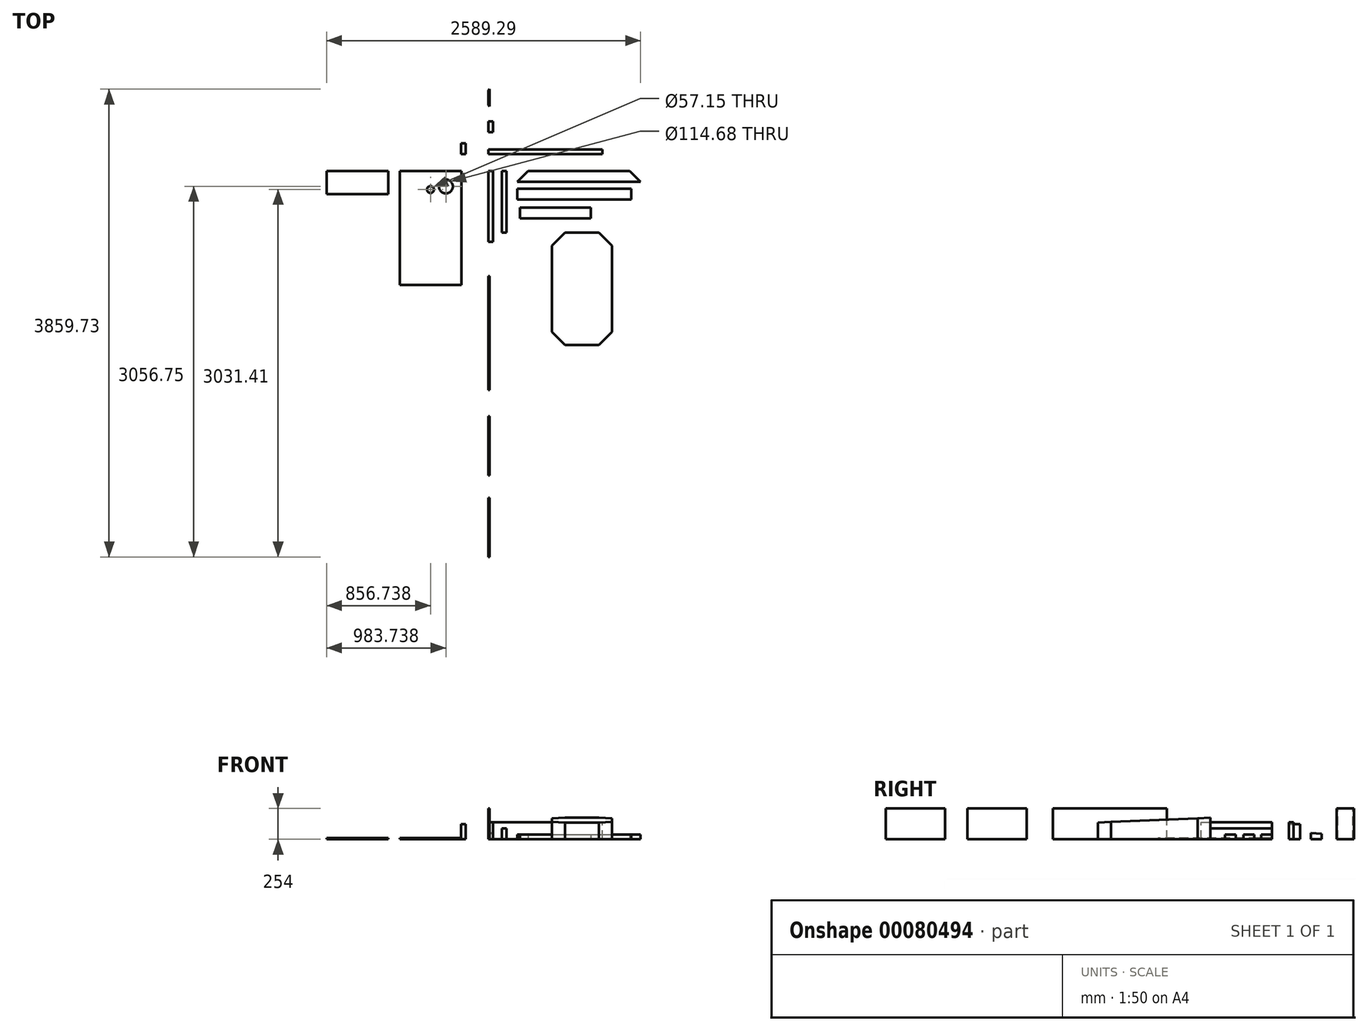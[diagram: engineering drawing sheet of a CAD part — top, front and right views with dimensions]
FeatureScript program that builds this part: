
annotation { "Feature Type Name" : "Feature", "Feature Type Description" : "" }
export const myFeature = defineFeature(function(context is Context, id is Id, definition is map)
    precondition{}
    {
        {
            var Q0;
            Q0=qCreatedBy(makeId("Front.planeOp"),FACE);
            var sketch = newSketch(context, id + "F0", { "sketchPlane" : qUnion([Q0])});
            skLineSegment(sketch, "E0.bottom", {"start": v(0, 0) * mm, "end": v(38.1, 0) * mm});
            skLineSegment(sketch, "E0.top", {"start": v(0, 139.7) * mm, "end": v(38.1, 139.7) * mm});
            skLineSegment(sketch, "E0.left", {"start": v(0, 0) * mm, "end": v(0, 139.7) * mm});
            skLineSegment(sketch, "E0.right", {"start": v(38.1, 0) * mm, "end": v(38.1, 139.7) * mm});
            skSolve(sketch);
        }
        {
            var Q0;
            Q0=makeQuery(id+"F0.imprint","IMPRINT",FACE,{"disambiguationData":[TD([[makeQuery(id+"F0.imprint","IMPRINT",EDGE,{"derivedFrom":sQuery(id+"F0.wireOp",EDGE,"E0.bottom")}),1.0]])]});
            extrude(context, id + "F1", {"entities" : qUnion([Q0]), "depth" : 584.2 * mm});
        }
        {
            var Q0;
            Q0=qCreatedBy(makeId("Right.planeOp"),FACE);
            var sketch = newSketch(context, id + "F2", { "sketchPlane" : qUnion([Q0])});
            skLineSegment(sketch, "E1.bottom", {"start": v(138.59, 0) * mm, "end": v(176.69, 0) * mm});
            skLineSegment(sketch, "E1.top", {"start": v(138.59, 139.7) * mm, "end": v(176.69, 139.7) * mm});
            skLineSegment(sketch, "E1.left", {"start": v(138.59, 0) * mm, "end": v(138.59, 139.7) * mm});
            skLineSegment(sketch, "E1.right", {"start": v(176.69, 0) * mm, "end": v(176.69, 139.7) * mm});
            skSolve(sketch);
        }
        {
            var Q0;
            Q0=makeQuery(id+"F2.imprint","IMPRINT",FACE,{"disambiguationData":[TD([[makeQuery(id+"F2.imprint","IMPRINT",EDGE,{"derivedFrom":sQuery(id+"F2.wireOp",EDGE,"E1.bottom")}),1.0]])]});
            extrude(context, id + "F3", {"entities" : qUnion([Q0]), "depth" : 939.8 * mm});
        }
        {
            var Q0;
            Q0=qCreatedBy(makeId("Front.planeOp"),FACE);
            var sketch = newSketch(context, id + "F4", { "sketchPlane" : qUnion([Q0])});
            skLineSegment(sketch, "E2.bottom", {"start": v(110.06, 0) * mm, "end": v(148.16, 0) * mm});
            skLineSegment(sketch, "E2.top", {"start": v(110.06, 88.9) * mm, "end": v(148.16, 88.9) * mm});
            skLineSegment(sketch, "E2.left", {"start": v(110.06, 0) * mm, "end": v(110.06, 88.9) * mm});
            skLineSegment(sketch, "E2.right", {"start": v(148.16, 0) * mm, "end": v(148.16, 88.9) * mm});
            skSolve(sketch);
        }
        {
            var Q0;
            Q0=makeQuery(id+"F4.imprint","IMPRINT",FACE,{"disambiguationData":[TD([[makeQuery(id+"F4.imprint","IMPRINT",EDGE,{"derivedFrom":sQuery(id+"F4.wireOp",EDGE,"E2.bottom")}),1.0]])]});
            extrude(context, id + "F5", {"entities" : qUnion([Q0]), "depth" : 508 * mm});
        }
        {
            var Q0;
            Q0=qCreatedBy(makeId("Top.planeOp"),FACE);
            var sketch = newSketch(context, id + "F6", { "sketchPlane" : qUnion([Q0])});
            skLineSegment(sketch, "E3.bottom", {"start": v(-224.08, 0) * mm, "end": v(-732.08, 0) * mm});
            skLineSegment(sketch, "E3.top", {"start": v(-224.08, -939.8) * mm, "end": v(-732.08, -939.8) * mm});
            skLineSegment(sketch, "E3.left", {"start": v(-224.08, 0) * mm, "end": v(-224.08, -939.8) * mm});
            skLineSegment(sketch, "E3.right", {"start": v(-732.08, 0) * mm, "end": v(-732.08, -939.8) * mm});
            skSolve(sketch);
        }
        {
            var Q0;
            Q0=makeQuery(id+"F6.imprint","IMPRINT",FACE,{"disambiguationData":[TD([[makeQuery(id+"F6.imprint","IMPRINT",EDGE,{"derivedFrom":sQuery(id+"F6.wireOp",EDGE,"E3.bottom")}),1.0]])]});
            extrude(context, id + "F7", {"entities" : qUnion([Q0]), "depth" : 9.52 * mm});
        }
        {
            var Q0;
            Q0=qCreatedBy(makeId("Top.planeOp"),FACE);
            var sketch = newSketch(context, id + "F8", { "sketchPlane" : qUnion([Q0])});
            skLineSegment(sketch, "E4.bottom", {"start": v(-826.82, 0) * mm, "end": v(-1334.82, 0) * mm});
            skLineSegment(sketch, "E4.top", {"start": v(-826.82, -190.5) * mm, "end": v(-1334.82, -190.5) * mm});
            skLineSegment(sketch, "E4.left", {"start": v(-826.82, 0) * mm, "end": v(-826.82, -190.5) * mm});
            skLineSegment(sketch, "E4.right", {"start": v(-1334.82, 0) * mm, "end": v(-1334.82, -190.5) * mm});
            skSolve(sketch);
        }
        {
            var Q0;
            Q0=makeQuery(id+"F8.imprint","IMPRINT",FACE,{"disambiguationData":[TD([[makeQuery(id+"F8.imprint","IMPRINT",EDGE,{"derivedFrom":sQuery(id+"F8.wireOp",EDGE,"E4.bottom")}),1.0]])]});
            extrude(context, id + "F9", {"entities" : qUnion([Q0]), "depth" : 9.52 * mm});
        }
        {
            var Q0;
            Q0=qCreatedBy(makeId("Right.planeOp"),FACE);
            var sketch = newSketch(context, id + "F10", { "sketchPlane" : qUnion([Q0])});
            skLineSegment(sketch, "E5", {"start": v(-866.98, 0) * mm, "end": v(-866.98, 254) * mm});
            skLineSegment(sketch, "E6", {"start": v(-866.98, 254) * mm, "end": v(-1806.78, 254) * mm});
            skLineSegment(sketch, "E7", {"start": v(-1806.78, 254) * mm, "end": v(-1806.78, 0) * mm});
            skLineSegment(sketch, "E8", {"start": v(-1806.78, 0) * mm, "end": v(-1616.28, 0) * mm});
            skLineSegment(sketch, "E9", {"start": v(-1616.28, 0) * mm, "end": v(-1616.28, 0) * mm});
            skLineSegment(sketch, "E10", {"start": v(-1616.28, 0) * mm, "end": v(-866.98, 0) * mm});
            skSolve(sketch);
        }
        {
            var Q0;
            Q0=makeQuery(id+"F10.imprint","IMPRINT",FACE,{"disambiguationData":[TD([[makeQuery(id+"F10.imprint","IMPRINT",EDGE,{"derivedFrom":sQuery(id+"F10.wireOp",EDGE,"E5")}),1.0]])]});
            extrude(context, id + "F11", {"entities" : qUnion([Q0]), "depth" : 9.52 * mm});
        }
        {
            var Q0;
            Q0=qCreatedBy(makeId("Right.planeOp"),FACE);
            var sketch = newSketch(context, id + "F12", { "sketchPlane" : qUnion([Q0])});
            skLineSegment(sketch, "E11.bottom", {"start": v(-2022.5, 0) * mm, "end": v(-2511.45, 0) * mm});
            skLineSegment(sketch, "E11.top", {"start": v(-2022.5, 254) * mm, "end": v(-2511.45, 254) * mm});
            skLineSegment(sketch, "E11.left", {"start": v(-2022.5, 0) * mm, "end": v(-2022.5, 254) * mm});
            skLineSegment(sketch, "E11.right", {"start": v(-2511.45, 0) * mm, "end": v(-2511.45, 254) * mm});
            skSolve(sketch);
        }
        {
            var Q0;
            Q0=makeQuery(id+"F12.imprint","IMPRINT",FACE,{"disambiguationData":[TD([[makeQuery(id+"F12.imprint","IMPRINT",EDGE,{"derivedFrom":sQuery(id+"F12.wireOp",EDGE,"E11.bottom")}),-1.0]])]});
            extrude(context, id + "F13", {"entities" : qUnion([Q0]), "depth" : 9.52 * mm});
        }
        {
            var Q0;
            Q0=qCreatedBy(makeId("Right.planeOp"),FACE);
            var sketch = newSketch(context, id + "F14", { "sketchPlane" : qUnion([Q0])});
            skLineSegment(sketch, "E12.bottom", {"start": v(-2694.8, 0) * mm, "end": v(-3183.75, 0) * mm});
            skLineSegment(sketch, "E12.top", {"start": v(-2694.8, 254) * mm, "end": v(-3183.75, 254) * mm});
            skLineSegment(sketch, "E12.left", {"start": v(-2694.8, 0) * mm, "end": v(-2694.8, 254) * mm});
            skLineSegment(sketch, "E12.right", {"start": v(-3183.75, 0) * mm, "end": v(-3183.75, 254) * mm});
            skSolve(sketch);
        }
        {
            var Q0;
            Q0=makeQuery(id+"F14.imprint","IMPRINT",FACE,{"disambiguationData":[TD([[makeQuery(id+"F14.imprint","IMPRINT",EDGE,{"derivedFrom":sQuery(id+"F14.wireOp",EDGE,"E12.bottom")}),-1.0]])]});
            extrude(context, id + "F15", {"entities" : qUnion([Q0]), "depth" : 9.52 * mm});
        }
        {
            var Q0;
            Q0=qCreatedBy(makeId("Top.planeOp"),FACE);
            var sketch = newSketch(context, id + "F16", { "sketchPlane" : qUnion([Q0])});
            skLineSegment(sketch, "E13.bottom", {"start": v(327.37, 0) * mm, "end": v(1165.57, 0) * mm});
            skLineSegment(sketch, "E13.top", {"start": v(238.47, -88.9) * mm, "end": v(1254.47, -88.9) * mm});
            skLineSegment(sketch, "E14", {"start": v(238.47, -88.9) * mm, "end": v(327.37, 0) * mm});
            skLineSegment(sketch, "E15", {"start": v(1254.47, -88.9) * mm, "end": v(1165.57, 0) * mm});
            skSolve(sketch);
        }
        {
            var Q0;
            Q0=makeQuery(id+"F16.imprint","IMPRINT",FACE,{"disambiguationData":[TD([[makeQuery(id+"F16.imprint","IMPRINT",EDGE,{"derivedFrom":sQuery(id+"F16.wireOp",EDGE,"E13.bottom")}),-1.0]])]});
            extrude(context, id + "F17", {"entities" : qUnion([Q0]), "depth" : 38.1 * mm});
        }
        {
            var Q0;
            Q0=qCreatedBy(makeId("Top.planeOp"),FACE);
            var sketch = newSketch(context, id + "F18", { "sketchPlane" : qUnion([Q0])});
            skLineSegment(sketch, "E16.bottom", {"start": v(238.93, -146.3) * mm, "end": v(1178.73, -146.3) * mm});
            skLineSegment(sketch, "E16.top", {"start": v(238.93, -235.2) * mm, "end": v(1178.73, -235.2) * mm});
            skLineSegment(sketch, "E16.left", {"start": v(238.93, -146.3) * mm, "end": v(238.93, -235.2) * mm});
            skLineSegment(sketch, "E16.right", {"start": v(1178.73, -146.3) * mm, "end": v(1178.73, -235.2) * mm});
            skSolve(sketch);
        }
        {
            var Q0;
            Q0=makeQuery(id+"F18.imprint","IMPRINT",FACE,{"disambiguationData":[TD([[makeQuery(id+"F18.imprint","IMPRINT",EDGE,{"derivedFrom":sQuery(id+"F18.wireOp",EDGE,"E16.bottom")}),-1.0]])]});
            extrude(context, id + "F19", {"entities" : qUnion([Q0]), "depth" : 38.1 * mm});
        }
        {
            var Q0;
            Q0=qCreatedBy(makeId("Top.planeOp"),FACE);
            var sketch = newSketch(context, id + "F20", { "sketchPlane" : qUnion([Q0])});
            skLineSegment(sketch, "E17.bottom", {"start": v(260.45, -300.02) * mm, "end": v(844.65, -300.02) * mm});
            skLineSegment(sketch, "E17.top", {"start": v(260.45, -388.92) * mm, "end": v(844.65, -388.92) * mm});
            skLineSegment(sketch, "E17.left", {"start": v(260.45, -300.02) * mm, "end": v(260.45, -388.92) * mm});
            skLineSegment(sketch, "E17.right", {"start": v(844.65, -300.02) * mm, "end": v(844.65, -388.92) * mm});
            skSolve(sketch);
        }
        {
            var Q0;
            Q0=makeQuery(id+"F20.imprint","IMPRINT",FACE,{"disambiguationData":[TD([[makeQuery(id+"F20.imprint","IMPRINT",EDGE,{"derivedFrom":sQuery(id+"F20.wireOp",EDGE,"E17.bottom")}),-1.0]])]});
            extrude(context, id + "F21", {"entities" : qUnion([Q0]), "depth" : 38.1 * mm});
        }
        {
            var Q0;
            Q0=qCreatedBy(makeId("Top.planeOp"),FACE);
            var sketch = newSketch(context, id + "F22", { "sketchPlane" : qUnion([Q0])});
            skLineSegment(sketch, "E18.bottom", {"start": v(-225.09, 141) * mm, "end": v(-186.99, 141) * mm});
            skLineSegment(sketch, "E18.top", {"start": v(-225.09, 229.9) * mm, "end": v(-186.99, 229.9) * mm});
            skLineSegment(sketch, "E18.left", {"start": v(-225.09, 141) * mm, "end": v(-225.09, 229.9) * mm});
            skLineSegment(sketch, "E18.right", {"start": v(-186.99, 141) * mm, "end": v(-186.99, 229.9) * mm});
            skSolve(sketch);
        }
        {
            var Q0;
            Q0=makeQuery(id+"F22.imprint","IMPRINT",FACE,{"disambiguationData":[TD([[makeQuery(id+"F22.imprint","IMPRINT",EDGE,{"derivedFrom":sQuery(id+"F22.wireOp",EDGE,"E18.bottom")}),1.0]])]});
            extrude(context, id + "F23", {"entities" : qUnion([Q0]), "depth" : 123.82 * mm});
        }
        {
            var Q0;
            Q0=qCreatedBy(makeId("Right.planeOp"),FACE);
            var sketch = newSketch(context, id + "F24", { "sketchPlane" : qUnion([Q0])});
            skLineSegment(sketch, "E19", {"start": v(320.73, 0) * mm, "end": v(320.73, 50.8) * mm});
            skLineSegment(sketch, "E20", {"start": v(320.73, 50.8) * mm, "end": v(409.63, 47.07) * mm});
            skLineSegment(sketch, "E21", {"start": v(409.63, 47.07) * mm, "end": v(409.63, 0) * mm});
            skLineSegment(sketch, "E22", {"start": v(409.63, 0) * mm, "end": v(320.73, 0) * mm});
            skSolve(sketch);
        }
        {
            var Q0;
            Q0=makeQuery(id+"F24.imprint","IMPRINT",FACE,{"disambiguationData":[TD([[makeQuery(id+"F24.imprint","IMPRINT",EDGE,{"derivedFrom":sQuery(id+"F24.wireOp",EDGE,"E19")}),-1.0]])]});
            extrude(context, id + "F25", {"entities" : qUnion([Q0]), "depth" : 38.1 * mm});
        }
        {
            var Q0;
            Q0=qCreatedBy(makeId("Right.planeOp"),FACE);
            var sketch = newSketch(context, id + "F26", { "sketchPlane" : qUnion([Q0])});
            skLineSegment(sketch, "E23.bottom", {"start": v(532.29, 0) * mm, "end": v(675.98, 0) * mm});
            skLineSegment(sketch, "E23.top", {"start": v(532.29, 254) * mm, "end": v(675.98, 254) * mm});
            skLineSegment(sketch, "E23.left", {"start": v(532.29, 0) * mm, "end": v(532.29, 254) * mm});
            skLineSegment(sketch, "E23.right", {"start": v(675.98, 0) * mm, "end": v(675.98, 254) * mm});
            skSolve(sketch);
        }
        {
            var Q0;
            Q0=makeQuery(id+"F26.imprint","IMPRINT",FACE,{"disambiguationData":[TD([[makeQuery(id+"F26.imprint","IMPRINT",EDGE,{"derivedFrom":sQuery(id+"F26.wireOp",EDGE,"E23.bottom")}),1.0]])]});
            extrude(context, id + "F27", {"entities" : qUnion([Q0]), "depth" : 9.52 * mm});
        }
        {
            var Q0;
            Q0=makeQuery(id+"F27.opExtrude","SWEPT_FACE",FACE,{"disambiguationData":[OSD([sQuery(id+"F26.wireOp",EDGE,"E23.top")])]});
            var sketch = newSketch(context, id + "F28", { "sketchPlane" : qUnion([Q0])});
            skLineSegment(sketch, "E24", {"start": v(9.53, 675.98) * mm, "end": v(0, 666.45) * mm});
            skLineSegment(sketch, "E25", {"start": v(0, 666.45) * mm, "end": v(0, 675.98) * mm});
            skLineSegment(sketch, "E26", {"start": v(0, 675.98) * mm, "end": v(9.53, 675.98) * mm});
            skLineSegment(sketch, "E27", {"start": v(9.52, 532.29) * mm, "end": v(0, 541.81) * mm});
            skLineSegment(sketch, "E28", {"start": v(0, 541.81) * mm, "end": v(0, 532.29) * mm});
            skLineSegment(sketch, "E29", {"start": v(0, 532.29) * mm, "end": v(9.53, 532.29) * mm});
            skSolve(sketch);
        }
        {
            var Q0;
            Q0=makeQuery(id+"F28.imprint","IMPRINT",FACE,{"disambiguationData":[TD([[makeQuery(id+"F28.imprint","IMPRINT",EDGE,{"derivedFrom":sQuery(id+"F28.wireOp",EDGE,"E24")}),-1.0]])]});
            var Q1;
            Q1=makeQuery(id+"F28.imprint","IMPRINT",FACE,{"disambiguationData":[TD([[makeQuery(id+"F28.imprint","IMPRINT",EDGE,{"derivedFrom":sQuery(id+"F28.wireOp",EDGE,"E27")}),1.0]])]});
            extrude(context, id + "F29", {"entities" : qUnion([Q0, Q1]), "operationType" : NewBodyOperationType.REMOVE, "oppositeDirection" : true, "depth" : 254 * mm});
        }
        {
            var Q0;
            Q0=makeQuery(id+"F7.opExtrude","CAP_EDGE",EDGE,{"disambiguationData":[OSD([sQuery(id+"F6.wireOp",EDGE,"E3.top")])],"isStart":false});
            cPlane(context, id + "F30", {"entities" : qUnion([Q0]), "cplaneType" : CPlaneType.LINE_ANGLE, "offset" : 152.4 * mm, "angle" : 87.6 * degree, "width" : 152.4 * mm, "height" : 152.4 * mm});
        }
        {
            var Q0;
            Q0=qCreatedBy(id+"F30.planeOp",FACE);
            var sketch = newSketch(context, id + "F31", { "sketchPlane" : qUnion([Q0])});
            skCircle(sketch, "E30", {"center": v(-478.08, -152) * mm, "radius": 28.58 * mm});
            skSolve(sketch);
        }
        {
            var Q0;
            Q0=makeQuery(id+"F31.imprint","IMPRINT",FACE,{"disambiguationData":[TD([[makeQuery(id+"F31.imprint","IMPRINT",EDGE,{"derivedFrom":sQuery(id+"F31.wireOp",EDGE,"E30")}),1.0]])]});
            extrude(context, id + "F32", {"entities" : qUnion([Q0]), "operationType" : NewBodyOperationType.REMOVE, "oppositeDirection" : true, "depth" : 76.2 * mm});
        }
        {
            var Q0;
            Q0=makeQuery(id+"F7.opExtrude","CAP_FACE",FACE,{"disambiguationData":[OSD([sQuery(id+"F6.wireOp",EDGE,"E3.bottom"),sQuery(id+"F6.wireOp",EDGE,"E3.top"),sQuery(id+"F6.wireOp",EDGE,"E3.left"),sQuery(id+"F6.wireOp",EDGE,"E3.right")])],"isStart":false});
            var sketch = newSketch(context, id + "F33", { "sketchPlane" : qUnion([Q0])});
            skCircle(sketch, "E31", {"center": v(-351.08, -127) * mm, "radius": 57.34 * mm});
            skSolve(sketch);
        }
        {
            var Q0;
            Q0=makeQuery(id+"F33.imprint","IMPRINT",FACE,{"disambiguationData":[TD([[makeQuery(id+"F33.imprint","IMPRINT",EDGE,{"derivedFrom":sQuery(id+"F33.wireOp",EDGE,"E31")}),1.0]])]});
            extrude(context, id + "F34", {"entities" : qUnion([Q0]), "operationType" : NewBodyOperationType.REMOVE, "oppositeDirection" : true, "depth" : 25.4 * mm});
        }
        {
            var Q0;
            Q0=qCreatedBy(makeId("Top.planeOp"),FACE);
            var sketch = newSketch(context, id + "F35", { "sketchPlane" : qUnion([Q0])});
            skLineSegment(sketch, "E32.bottom", {"start": v(911.56, -507.12) * mm, "end": v(631.8, -507.12) * mm});
            skLineSegment(sketch, "E32.top", {"start": v(911.56, -1434.22) * mm, "end": v(631.8, -1434.22) * mm});
            skLineSegment(sketch, "E32.left", {"start": v(1019.33, -614.88) * mm, "end": v(1019.33, -1326.45) * mm});
            skLineSegment(sketch, "E32.right", {"start": v(524.03, -614.88) * mm, "end": v(524.03, -1326.45) * mm});
            skLineSegment(sketch, "E33", {"start": v(911.56, -507.12) * mm, "end": v(1019.33, -614.88) * mm});
            skLineSegment(sketch, "E34", {"start": v(631.8, -507.12) * mm, "end": v(524.03, -614.88) * mm});
            skLineSegment(sketch, "E35", {"start": v(524.03, -1326.45) * mm, "end": v(631.8, -1434.22) * mm});
            skLineSegment(sketch, "E36", {"start": v(1019.33, -1326.45) * mm, "end": v(911.56, -1434.22) * mm});
            skSolve(sketch);
        }
        {
            var Q0;
            Q0=makeQuery(id+"F35.imprint","IMPRINT",FACE,{"disambiguationData":[TD([[makeQuery(id+"F35.imprint","IMPRINT",EDGE,{"derivedFrom":sQuery(id+"F35.wireOp",EDGE,"E32.bottom")}),1.0]])]});
            extrude(context, id + "F36", {"entities" : qUnion([Q0]), "depth" : 177.8 * mm});
        }
        {
            var Q0;
            Q0=makeQuery(id+"F36.opExtrude","SWEPT_FACE",FACE,{"disambiguationData":[OSD([sQuery(id+"F35.wireOp",EDGE,"E32.left")])]});
            var sketch = newSketch(context, id + "F37", { "sketchPlane" : qUnion([Q0])});
            skLineSegment(sketch, "E37", {"start": v(-614.88, 177.8) * mm, "end": v(-504.71, 177.8) * mm});
            skLineSegment(sketch, "E38", {"start": v(-504.71, 177.8) * mm, "end": v(-1454.34, 138) * mm});
            skLineSegment(sketch, "E39", {"start": v(-614.88, 177.8) * mm, "end": v(-1456.63, 177.8) * mm});
            skLineSegment(sketch, "E40", {"start": v(-1456.63, 177.8) * mm, "end": v(-1454.34, 138) * mm});
            skSolve(sketch);
        }
        {
            var Q0;
            {var subQ0=sQuery(id+"F37.wireOp",EDGE,"E37");Q0=makeQuery(id+"F37.imprint","IMPRINT",FACE,{"disambiguationData":[TD([[makeQuery(id+"F37.imprint","IMPRINT",EDGE,{"derivedFrom":subQ0}),-1.0]])]});}
            var Q1;
            {var subQ0=sQuery(id+"F37.wireOp",EDGE,"E38");var subQ1=sQuery(id+"F35.wireOp",EDGE,"E32.left");var subQ2=makeQuery(id+"F36.opExtrude","SWEPT_EDGE",EDGE,{"disambiguationData":[OSD([subQ1,sQuery(id+"F35.wireOp",EDGE,"E33")])]});var subQ3=makeQuery(id+"F37.imprint","INTERSECT",VERTEX,{"derivedFrom":[subQ2,subQ0]});Q1=makeQuery(id+"F37.imprint","IMPRINT",FACE,{"disambiguationData":[TD([[makeQuery(id+"F37.imprint","IMPRINT",EDGE,{"disambiguationData":[TD([[subQ3,-1.0]])],"derivedFrom":subQ0}),-1.0]])]});}
            var Q2;
            {var subQ0=sQuery(id+"F37.wireOp",EDGE,"E40");Q2=makeQuery(id+"F37.imprint","IMPRINT",FACE,{"disambiguationData":[TD([[makeQuery(id+"F37.imprint","IMPRINT",EDGE,{"derivedFrom":subQ0}),1.0]])]});}
            extrude(context, id + "F38", {"entities" : qUnion([Q0, Q1, Q2]), "operationType" : NewBodyOperationType.REMOVE, "oppositeDirection" : true, "depth" : 508 * mm});
        }
    });
